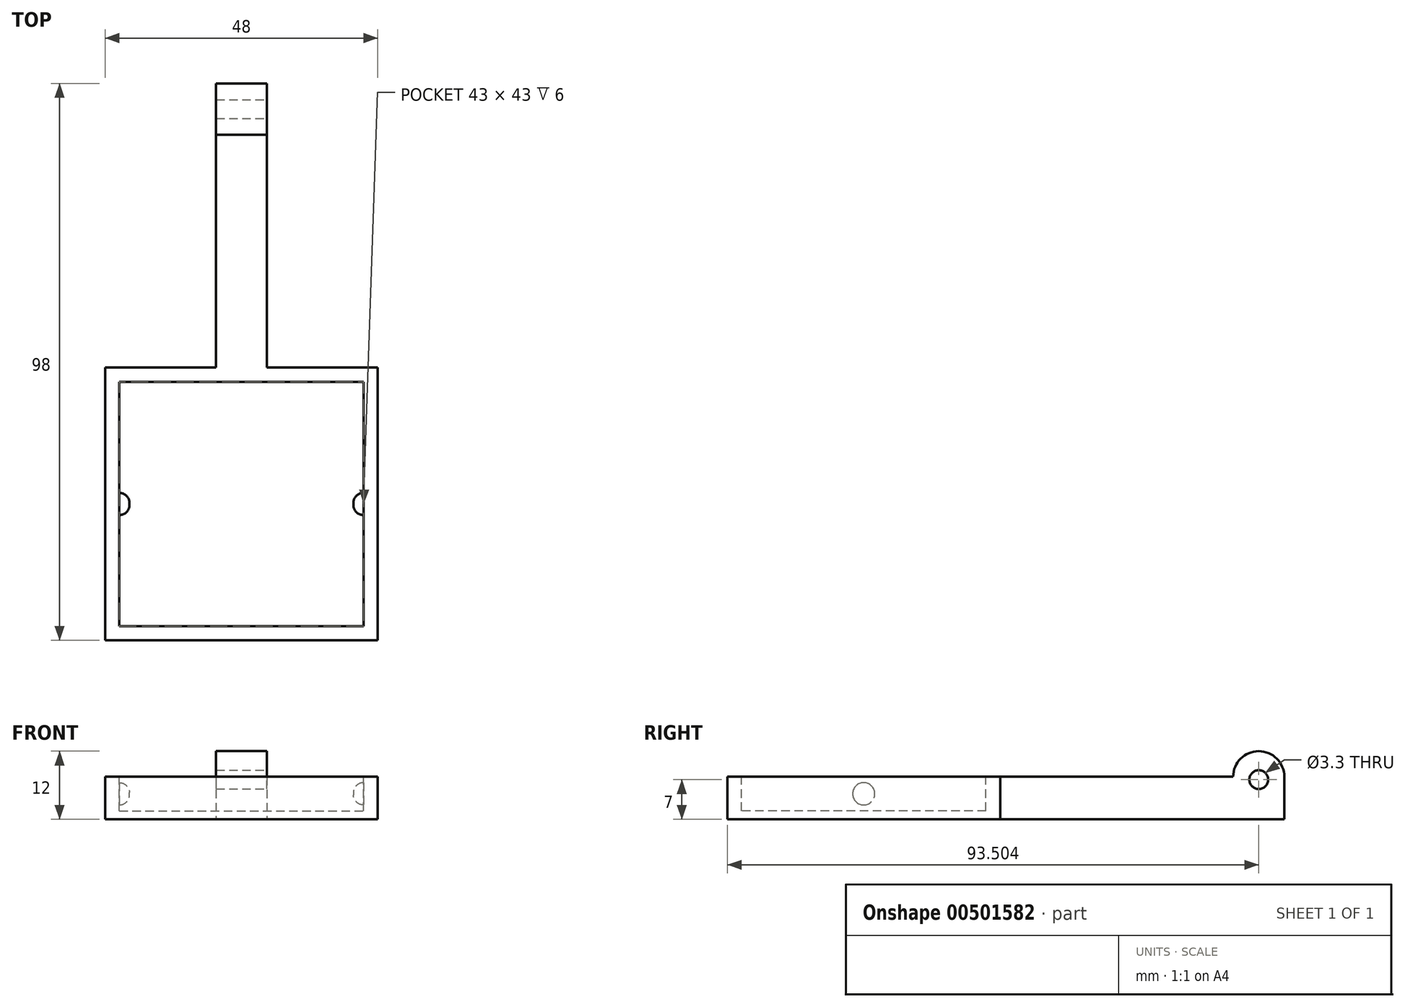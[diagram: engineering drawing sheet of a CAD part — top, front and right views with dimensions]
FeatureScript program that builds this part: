
annotation { "Feature Type Name" : "Feature", "Feature Type Description" : "" }
export const myFeature = defineFeature(function(context is Context, id is Id, definition is map)
    precondition{}
    {
        {
            var Q0;
            Q0=qCreatedBy(makeId("Top.planeOp"),FACE);
            var sketch = newSketch(context, id + "F0", { "sketchPlane" : qUnion([Q0])});
            skLineSegment(sketch, "E0.bottom", {"start": v(-24, -9.07) * mm, "end": v(24, -9.07) * mm});
            skLineSegment(sketch, "E0.top", {"start": v(-24, -57.07) * mm, "end": v(24, -57.07) * mm});
            skLineSegment(sketch, "E0.left", {"start": v(-24, -9.07) * mm, "end": v(-24, -57.07) * mm});
            skLineSegment(sketch, "E0.right", {"start": v(24, -9.07) * mm, "end": v(24, -57.07) * mm});
            skLineSegment(sketch, "E1.bottom", {"start": v(-4.45, -9.07) * mm, "end": v(4.45, -9.07) * mm});
            skLineSegment(sketch, "E1.top", {"start": v(-4.45, 40.93) * mm, "end": v(4.45, 40.93) * mm});
            skLineSegment(sketch, "E1.left", {"start": v(-4.45, -9.07) * mm, "end": v(-4.45, 40.93) * mm});
            skLineSegment(sketch, "E1.right", {"start": v(4.45, -9.07) * mm, "end": v(4.45, 40.93) * mm});
            skSolve(sketch);
        }
        {
            var Q0;
            Q0=qSketchRegion(id+"F0",true);
            extrude(context, id + "F1", {"entities" : qUnion([Q0]), "depth" : 7.5 * mm, "offsetDistance" : 25 * mm});
        }
        {
            var Q0;
            Q0=makeQuery(id+"F1.opExtrude","CAP_FACE",FACE,{"disambiguationData":[OSD([sQuery(id+"F0.wireOp",EDGE,"E0.bottom"),sQuery(id+"F0.wireOp",EDGE,"E0.top"),sQuery(id+"F0.wireOp",EDGE,"E0.left"),sQuery(id+"F0.wireOp",EDGE,"E0.right"),sQuery(id+"F0.wireOp",EDGE,"E1.top"),sQuery(id+"F0.wireOp",EDGE,"E1.left"),sQuery(id+"F0.wireOp",EDGE,"E1.right")])],"isStart":false});
            var sketch = newSketch(context, id + "F2", { "sketchPlane" : qUnion([Q0])});
            skLineSegment(sketch, "E2.bottom", {"start": v(-21.5, -11.57) * mm, "end": v(21.5, -11.57) * mm});
            skLineSegment(sketch, "E2.top", {"start": v(-21.5, -54.57) * mm, "end": v(21.5, -54.57) * mm});
            skLineSegment(sketch, "E2.left", {"start": v(-21.5, -11.57) * mm, "end": v(-21.5, -54.57) * mm});
            skLineSegment(sketch, "E2.right", {"start": v(21.5, -11.57) * mm, "end": v(21.5, -54.57) * mm});
            skSolve(sketch);
        }
        {
            var Q0;
            Q0=qSketchRegion(id+"F2",true);
            extrude(context, id + "F3", {"entities" : qUnion([Q0]), "operationType" : NewBodyOperationType.REMOVE, "oppositeDirection" : true, "depth" : 6 * mm, "offsetDistance" : 25 * mm});
        }
        {
            var Q0;
            Q0=makeQuery(id+"F1.opExtrude","CAP_FACE",FACE,{"disambiguationData":[OSD([sQuery(id+"F0.wireOp",EDGE,"E0.bottom"),sQuery(id+"F0.wireOp",EDGE,"E0.top"),sQuery(id+"F0.wireOp",EDGE,"E0.left"),sQuery(id+"F0.wireOp",EDGE,"E0.right"),sQuery(id+"F0.wireOp",EDGE,"E1.top"),sQuery(id+"F0.wireOp",EDGE,"E1.left"),sQuery(id+"F0.wireOp",EDGE,"E1.right")])],"isStart":false});
            var sketch = newSketch(context, id + "F4", { "sketchPlane" : qUnion([Q0])});
            skLineSegment(sketch, "E3.bottom", {"start": v(-4.45, 40.93) * mm, "end": v(4.45, 40.93) * mm});
            skLineSegment(sketch, "E3.top", {"start": v(-4.45, 31.93) * mm, "end": v(4.45, 31.93) * mm});
            skLineSegment(sketch, "E3.left", {"start": v(-4.45, 40.93) * mm, "end": v(-4.45, 31.93) * mm});
            skLineSegment(sketch, "E3.right", {"start": v(4.45, 40.93) * mm, "end": v(4.45, 31.93) * mm});
            skSolve(sketch);
        }
        {
            var Q0;
            Q0=qSketchRegion(id+"F4",true);
            extrude(context, id + "F5", {"entities" : qUnion([Q0]), "operationType" : NewBodyOperationType.ADD, "depth" : 4.5 * mm, "offsetDistance" : 25 * mm});
        }
        {
            var Q0;
            Q0=makeQuery(id+"F5.opExtrude","CAP_EDGE",EDGE,{"disambiguationData":[OSD([sQuery(id+"F4.wireOp",EDGE,"QDJ7WwMm-5TQc-SNhG-ZZcw-lrSSIwrfsWDn.top")])],"isStart":false});
            var Q1;
            Q1=makeQuery(id+"F5.opExtrude","CAP_EDGE",EDGE,{"disambiguationData":[OSD([sQuery(id+"F4.wireOp",EDGE,"QDJ7WwMm-5TQc-SNhG-ZZcw-lrSSIwrfsWDn.bottom")])],"isStart":false});
            var Q2;
            Q2=makeQuery(id+"F5.opExtrude","CAP_EDGE",EDGE,{"disambiguationData":[OSD([sQuery(id+"F4.wireOp",EDGE,"E3.bottom")])],"isStart":false});
            var Q3;
            Q3=makeQuery(id+"F5.opExtrude","CAP_EDGE",EDGE,{"disambiguationData":[OSD([sQuery(id+"F4.wireOp",EDGE,"E3.top")])],"isStart":false});
            fillet(context, id + "F6", {"entities" : qUnion([Q0, Q1, Q2, Q3]), "radius" : 4.5 * mm, "tangentPropagation" : true, "allowEdgeOverflow" : false});
        }
        {
            var Q0;
            Q0=makeQuery(id+"F3.boolean.opBoolean","COPY",FACE,{"derivedFrom":makeQuery(id+"F3.opExtrude","SWEPT_FACE",FACE,{"disambiguationData":[OSD([sQuery(id+"F2.wireOp",EDGE,"E2.right")])]})});
            var sketch = newSketch(context, id + "F7", { "sketchPlane" : qUnion([Q0])});
            skCircle(sketch, "E4", {"center": v(33.07, 4.5) * mm, "radius": 1.95 * mm});
            skPoint(sketch, "E4.centerSnap0", {"position": v(33.07, 7.5) * mm});
            skSolve(sketch);
        }
        {
            var Q0;
            Q0 = qSketchRegion(id + "F7", true);
            extrude(context, id + "F8", {"entities" : qUnion([Q0]), "operationType" : NewBodyOperationType.ADD, "depth" : 1.8 * mm, "offsetDistance" : 25 * mm});
        }
        {
            var Q0;
            Q0=makeQuery(id+"F3.boolean.opBoolean","COPY",FACE,{"derivedFrom":makeQuery(id+"F3.opExtrude","SWEPT_FACE",FACE,{"disambiguationData":[OSD([sQuery(id+"F2.wireOp",EDGE,"E2.left")])]})});
            var sketch = newSketch(context, id + "F9", { "sketchPlane" : qUnion([Q0])});
            skCircle(sketch, "E5", {"center": v(-33.07, 4.5) * mm, "radius": 1.95 * mm});
            skPoint(sketch, "E5.centerSnap0", {"position": v(-33.07, 7.5) * mm});
            skSolve(sketch);
        }
        {
            var Q0;
            Q0 = qSketchRegion(id + "F9", true);
            extrude(context, id + "F10", {"entities" : qUnion([Q0]), "operationType" : NewBodyOperationType.ADD, "depth" : 1.8 * mm, "offsetDistance" : 25 * mm});
        }
        {
            var Q0;
            Q0=makeQuery(id+"F5.boolean.opBoolean","MERGE",FACE,{"derivedFrom":[makeQuery(id+"F1.opExtrude","SWEPT_FACE",FACE,{"disambiguationData":[OSD([sQuery(id+"F0.wireOp",EDGE,"E1.right")])]}),makeQuery(id+"F5.opExtrude","SWEPT_FACE",FACE,{"disambiguationData":[OSD([sQuery(id+"F4.wireOp",EDGE,"E3.right")])]})]});
            var sketch = newSketch(context, id + "F11", { "sketchPlane" : qUnion([Q0])});
            skPoint(sketch, "E6", {"position": v(36.43, 7) * mm});
            skPoint(sketch, "E6.positionSnap0", {"position": v(36.43, 12) * mm});
            skSolve(sketch);
        }
        {
            var Q0;
            Q0=sQuery(id+"F11.wireOp",VERTEX,"E6");
            var Q1;
            Q1=makeQuery(id+"F1.opExtrude","SWEPT_BODY",BODY,{"disambiguationData":[OSD([sQuery(id+"F0.wireOp",EDGE,"E0.bottom"),sQuery(id+"F0.wireOp",EDGE,"E0.top"),sQuery(id+"F0.wireOp",EDGE,"E0.left"),sQuery(id+"F0.wireOp",EDGE,"E0.right"),sQuery(id+"F0.wireOp",EDGE,"E1.top"),sQuery(id+"F0.wireOp",EDGE,"E1.left"),sQuery(id+"F0.wireOp",EDGE,"E1.right")])]});
            hole(context, id + "F12", {"style" : HoleStyle.SIMPLE, "endStyle" : HoleEndStyle.THROUGH, "holeDiameter" : 3.3 * mm, "isTappedThrough" : true, "tappedDepth" : 12 * mm, "tapClearance" : 3, "startFromSketch" : true, "locations" : qUnion([Q0]), "scope" : qUnion([Q1])});
        }
        {
            var Q0;
            Q0=makeQuery(id+"F10.opExtrude","CAP_EDGE",EDGE,{"disambiguationData":[OSD([sQuery(id+"F9.wireOp",EDGE,"E5")])],"isStart":false});
            var Q1;
            Q1=makeQuery(id+"F8.opExtrude","CAP_EDGE",EDGE,{"disambiguationData":[OSD([sQuery(id+"F7.wireOp",EDGE,"E4")])],"isStart":false});
            fillet(context, id + "F13", {"entities" : qUnion([Q0, Q1]), "radius" : 1.75 * mm, "tangentPropagation" : true, "allowEdgeOverflow" : false});
        }
    });
